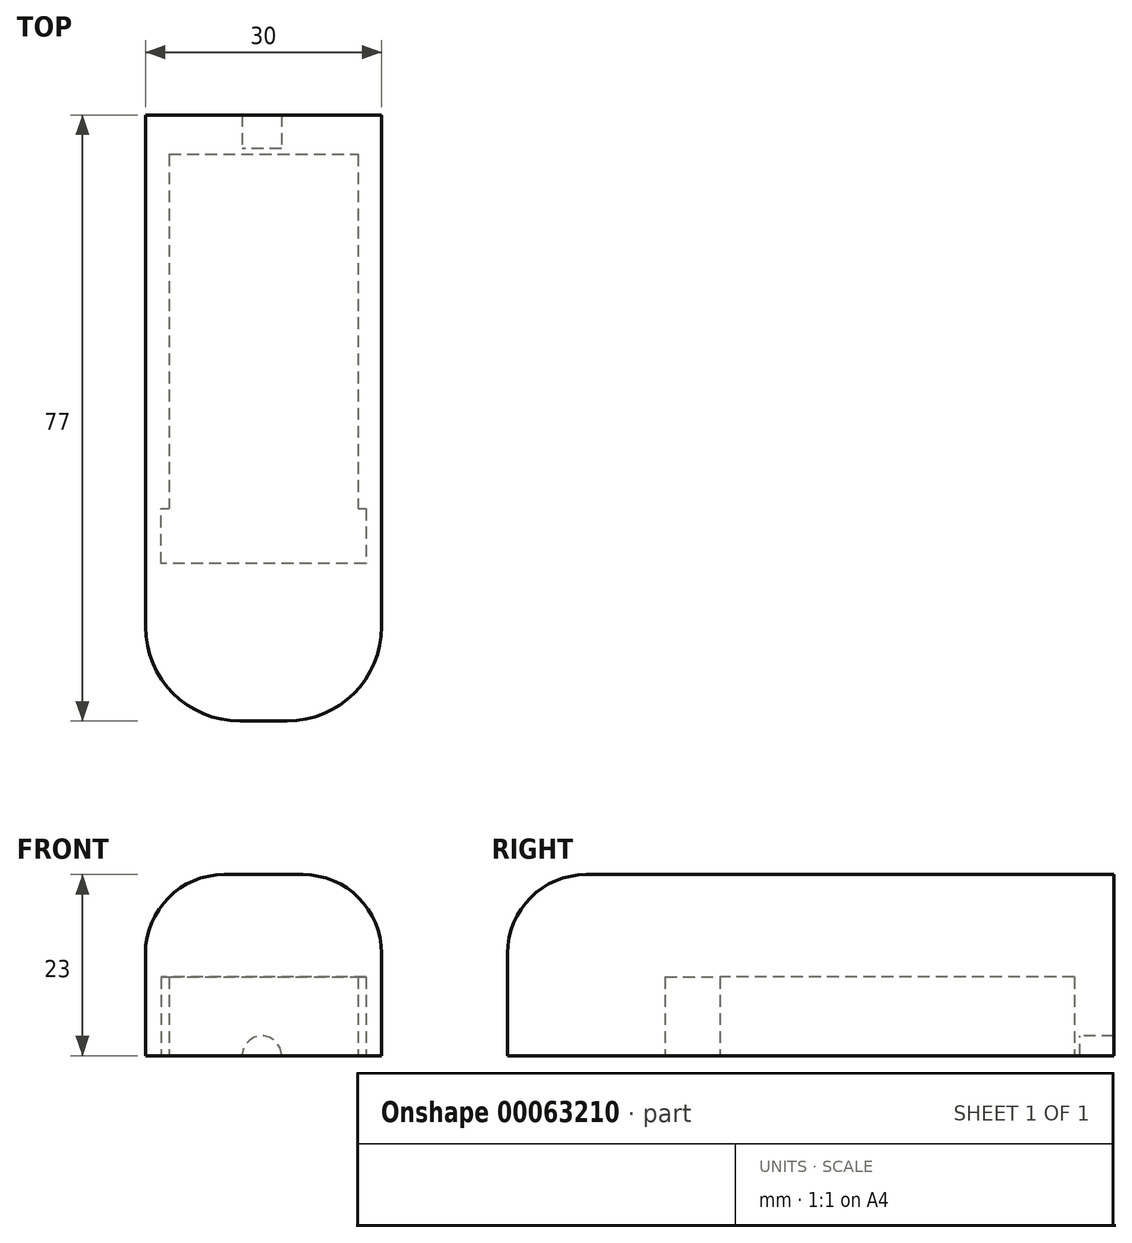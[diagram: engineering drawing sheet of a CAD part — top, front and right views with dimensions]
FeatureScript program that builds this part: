
annotation { "Feature Type Name" : "Feature", "Feature Type Description" : "" }
export const myFeature = defineFeature(function(context is Context, id is Id, definition is map)
    precondition{}
    {
        {
            var Q0;
            Q0=qCreatedBy(makeId("Top.planeOp"),FACE);
            var sketch = newSketch(context, id + "F0", { "sketchPlane" : qUnion([Q0])});
            skLineSegment(sketch, "E0", {"start": v(-25, -0.7) * mm, "end": v(-25, -45.7) * mm});
            skLineSegment(sketch, "E1", {"start": v(-25, -0.7) * mm, "end": v(-1, -0.7) * mm});
            skLineSegment(sketch, "E2", {"start": v(-1, -0.7) * mm, "end": v(-1, -45.7) * mm});
            skLineSegment(sketch, "E3", {"start": v(-1, -45.7) * mm, "end": v(0, -45.7) * mm});
            skLineSegment(sketch, "E4", {"start": v(0, -45.7) * mm, "end": v(0, -52.7) * mm});
            skLineSegment(sketch, "E5", {"start": v(0, -52.7) * mm, "end": v(-26, -52.7) * mm});
            skLineSegment(sketch, "E6", {"start": v(-26, -52.7) * mm, "end": v(-26, -45.7) * mm});
            skLineSegment(sketch, "E7", {"start": v(-26, -45.7) * mm, "end": v(-25, -45.7) * mm});
            skLineSegment(sketch, "E8", {"start": v(2, -60.7) * mm, "end": v(2, 4.3) * mm});
            skLineSegment(sketch, "E9", {"start": v(2, 4.3) * mm, "end": v(-28, 4.3) * mm});
            skLineSegment(sketch, "E10", {"start": v(-28, 4.3) * mm, "end": v(-28, -60.7) * mm});
            skLineSegment(sketch, "E11", {"start": v(-16, -72.7) * mm, "end": v(-10, -72.7) * mm});
            skPoint(sketch, "E12.visualSharp", {"position": v(2, -72.7) * mm});
            skArc(sketch, "E12.filletArc", {"start": v(-10, -72.7) * mm, "mid": v(-1.51, -69.18) * mm, "end": v(2, -60.7) * mm});
            skPoint(sketch, "E13.visualSharp", {"position": v(-28, -72.7) * mm});
            skArc(sketch, "E13.filletArc", {"start": v(-28, -60.7) * mm, "mid": v(-24.49, -69.18) * mm, "end": v(-16, -72.7) * mm});
            skSolve(sketch);
        }
        {
            var Q0;
            Q0=makeQuery(id+"F0.imprint","IMPRINT",FACE,{"disambiguationData":[TD([[makeQuery(id+"F0.imprint","IMPRINT",EDGE,{"derivedFrom":sQuery(id+"F0.wireOp",EDGE,"E0")}),-1.0]])]});
            extrude(context, id + "F1", {"entities" : qUnion([Q0]), "depth" : 23 * mm});
        }
        {
            var Q0;
            Q0=makeQuery(id+"F0.imprint","IMPRINT",FACE,{"disambiguationData":[TD([[makeQuery(id+"F0.imprint","IMPRINT",EDGE,{"derivedFrom":sQuery(id+"F0.wireOp",EDGE,"E0")}),1.0]])]});
            extrude(context, id + "F2", {"entities" : qUnion([Q0]), "operationType" : NewBodyOperationType.ADD, "depth" : 23 * mm});
        }
        {
            var Q0;
            Q0=makeQuery(id+"F0.imprint","IMPRINT",FACE,{"disambiguationData":[TD([[makeQuery(id+"F0.imprint","IMPRINT",EDGE,{"derivedFrom":sQuery(id+"F0.wireOp",EDGE,"E0")}),1.0]])]});
            extrude(context, id + "F3", {"entities" : qUnion([Q0]), "operationType" : NewBodyOperationType.REMOVE, "depth" : 10 * mm});
        }
        {
            var Q0;
            Q0=makeQuery(id+"F1.opExtrude","CAP_EDGE",EDGE,{"disambiguationData":[OSD([sQuery(id+"F0.wireOp",EDGE,"E10")])],"isStart":false});
            fillet(context, id + "F4", {"entities" : qUnion([Q0]), "radius" : 10 * mm, "tangentPropagation" : true, "allowEdgeOverflow" : false});
        }
        {
            var Q0;
            Q0=qCreatedBy(makeId("Front.planeOp"),FACE);
            var sketch = newSketch(context, id + "F5", { "sketchPlane" : qUnion([Q0])});
            skPoint(sketch, "E14", {"position": v(-13.2, 0) * mm});
            skSolve(sketch);
        }
        {
            var Q0;
            Q0=sQuery(id+"F5.wireOp",VERTEX,"E14");
            var Q1;
            Q1=makeQuery(id+"F1.opExtrude","SWEPT_BODY",BODY,{"disambiguationData":[OSD([sQuery(id+"F0.wireOp",EDGE,"E0"),sQuery(id+"F0.wireOp",EDGE,"E1"),sQuery(id+"F0.wireOp",EDGE,"E2"),sQuery(id+"F0.wireOp",EDGE,"E3"),sQuery(id+"F0.wireOp",EDGE,"E4"),sQuery(id+"F0.wireOp",EDGE,"E5"),sQuery(id+"F0.wireOp",EDGE,"E6"),sQuery(id+"F0.wireOp",EDGE,"E7"),sQuery(id+"F0.wireOp",EDGE,"E8"),sQuery(id+"F0.wireOp",EDGE,"E9"),sQuery(id+"F0.wireOp",EDGE,"E10"),sQuery(id+"F0.wireOp",EDGE,"E11"),sQuery(id+"F0.wireOp",EDGE,"E12.filletArc"),sQuery(id+"F0.wireOp",EDGE,"E13.filletArc")])]});
            hole(context, id + "F6", {"style" : HoleStyle.SIMPLE, "endStyle" : HoleEndStyle.THROUGH, "holeDiameter" : 5 * mm, "isTappedThrough" : true, "tappedDepth" : 12 * mm, "tapClearance" : 3, "startFromSketch" : true, "locations" : qUnion([Q0]), "scope" : qUnion([Q1])});
        }
    });
